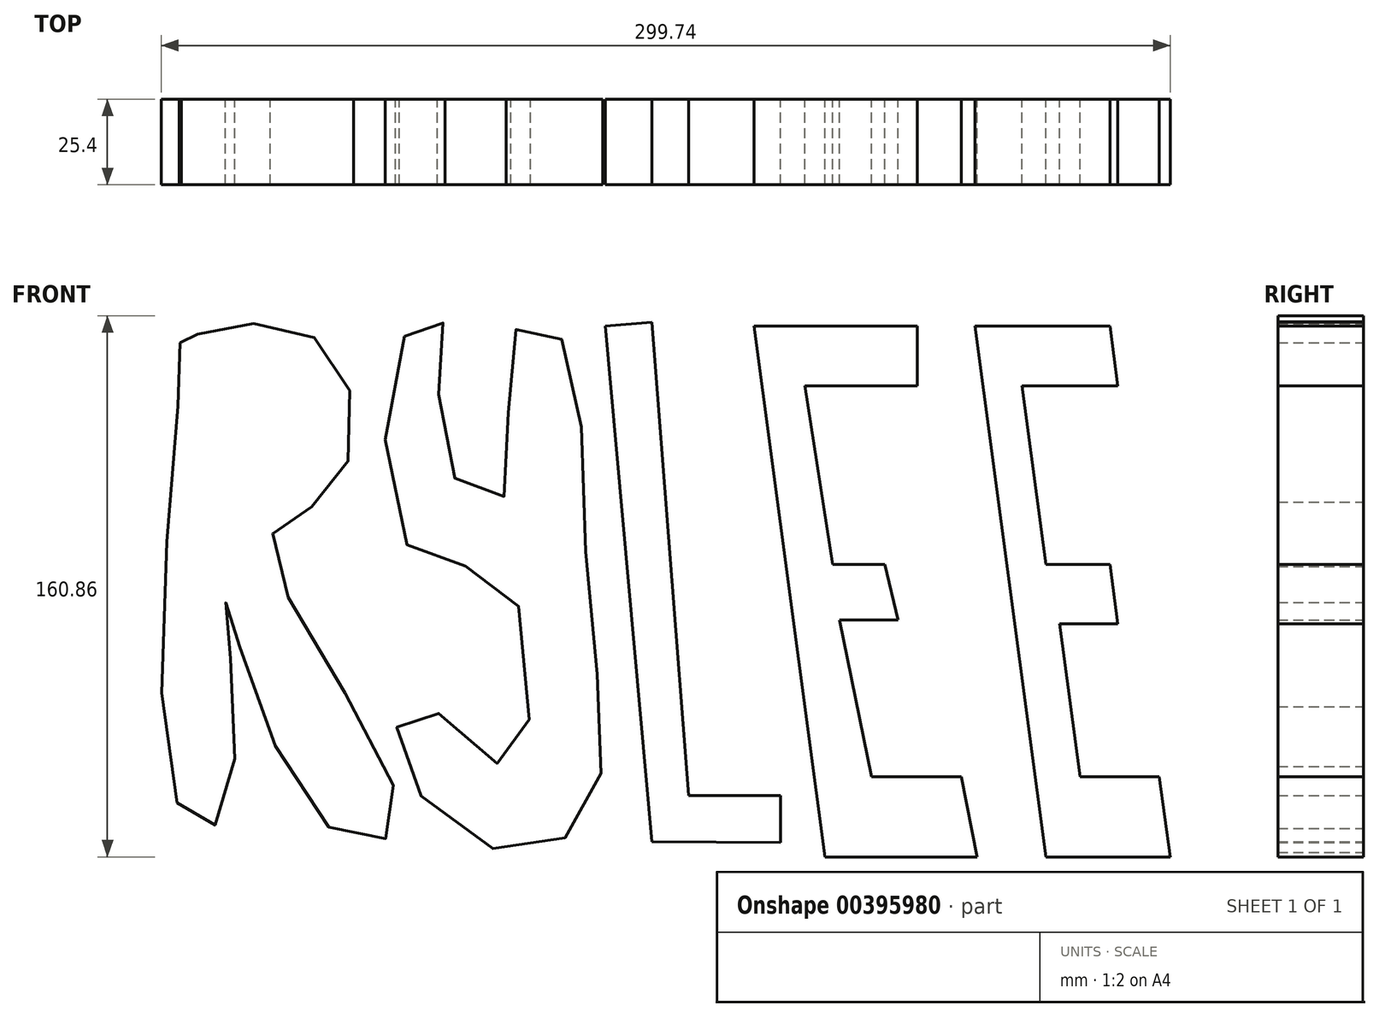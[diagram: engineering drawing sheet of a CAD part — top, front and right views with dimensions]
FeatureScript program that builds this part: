
annotation { "Feature Type Name" : "Feature", "Feature Type Description" : "" }
export const myFeature = defineFeature(function(context is Context, id is Id, definition is map)
    precondition{}
    {
        {
            var Q0;
            Q0=qCreatedBy(makeId("Front.planeOp"),FACE);
            var sketch = newSketch(context, id + "F0", { "sketchPlane" : qUnion([Q0])});
            skFitSpline(sketch, "E0", {"points": [v(-146.74, -62.42) * mm, v(-145.75, 74.33) * mm, v(-146.08, 74.37) * mm, v(-136.19, 78.37) * mm, v(-100.9, 71.57) * mm, v(-100.9, 29.89) * mm, v(-119.04, 14.58) * mm, v(-80.79, -66.82) * mm, v(-103.54, -67.91) * mm, v(-132.23, -2.87) * mm, v(-132.56, -65.5) * mm, v(-146.74, -62.42) * mm]});
            skSolve(sketch);
        }
        {
            var Q0;
            Q0=qCreatedBy(makeId("Front.planeOp"),FACE);
            var sketch = newSketch(context, id + "F1", { "sketchPlane" : qUnion([Q0])});
            skFitSpline(sketch, "E1", {"points": [v(-79.14, 76.34) * mm, v(-75.18, 10.48) * mm, v(-49.8, 4.41) * mm, v(-47.15, -51.23) * mm, v(-71.89, -34.31) * mm, v(-81.78, -42.74) * mm, v(-53.75, -75.77) * mm, v(-24.07, -64.67) * mm, v(-24.73, 3.42) * mm, v(-33.96, 77.39) * mm, v(-47.15, 76.5) * mm, v(-49.8, 28.36) * mm, v(-67.93, 41.14) * mm, v(-67.93, 80.76) * mm, v(-79.14, 76.34) * mm]});
            skSolve(sketch);
        }
        {
            var Q0;
            Q0=qCreatedBy(makeId("Front.planeOp"),FACE);
            var sketch = newSketch(context, id + "F2", { "sketchPlane" : qUnion([Q0])});
            skLineSegment(sketch, "E2", {"start": v(-19.46, 79.29) * mm, "end": v(-5.6, -74.23) * mm});
            skLineSegment(sketch, "E3", {"start": v(-5.94, -73.9) * mm, "end": v(32.65, -74.23) * mm});
            skLineSegment(sketch, "E4", {"start": v(32.65, -74.23) * mm, "end": v(32.65, -60.17) * mm});
            skLineSegment(sketch, "E5", {"start": v(32.65, -60.17) * mm, "end": v(5.28, -60.17) * mm});
            skLineSegment(sketch, "E6", {"start": v(5.28, -60.17) * mm, "end": v(-5.6, 80.52) * mm});
            skLineSegment(sketch, "E7", {"start": v(-5.6, 80.52) * mm, "end": v(-19.46, 79.29) * mm});
            skLineSegment(sketch, "E8", {"start": v(24.73, 79.29) * mm, "end": v(45.84, -78.47) * mm});
            skLineSegment(sketch, "E9", {"start": v(45.84, -78.47) * mm, "end": v(91.01, -78.47) * mm});
            skLineSegment(sketch, "E10", {"start": v(91.01, -78.47) * mm, "end": v(86.4, -54.63) * mm});
            skLineSegment(sketch, "E11", {"start": v(86.4, -54.63) * mm, "end": v(59.68, -54.63) * mm});
            skLineSegment(sketch, "E12", {"start": v(59.68, -54.63) * mm, "end": v(50.12, -8.08) * mm});
            skLineSegment(sketch, "E13", {"start": v(50.12, -8.08) * mm, "end": v(67.6, -8.08) * mm});
            skLineSegment(sketch, "E14", {"start": v(67.6, -8.08) * mm, "end": v(63.64, 8.43) * mm});
            skLineSegment(sketch, "E15", {"start": v(63.64, 8.43) * mm, "end": v(48.14, 8.43) * mm});
            skLineSegment(sketch, "E16", {"start": v(48.14, 8.43) * mm, "end": v(39.9, 61.58) * mm});
            skLineSegment(sketch, "E17", {"start": v(39.9, 61.58) * mm, "end": v(73.2, 61.58) * mm});
            skLineSegment(sketch, "E18", {"start": v(73.2, 61.58) * mm, "end": v(73.2, 79.29) * mm});
            skLineSegment(sketch, "E19", {"start": v(73.2, 79.29) * mm, "end": v(24.73, 79.29) * mm});
            skLineSegment(sketch, "E20", {"start": v(90.35, 79.29) * mm, "end": v(111.46, -78.47) * mm});
            skLineSegment(sketch, "E21", {"start": v(111.46, -78.47) * mm, "end": v(148.39, -78.47) * mm});
            skLineSegment(sketch, "E22", {"start": v(148.39, -78.47) * mm, "end": v(145.2, -54.63) * mm});
            skLineSegment(sketch, "E23", {"start": v(145.2, -54.63) * mm, "end": v(121.68, -54.63) * mm});
            skLineSegment(sketch, "E24", {"start": v(121.68, -54.63) * mm, "end": v(115.6, -9.2) * mm});
            skLineSegment(sketch, "E25", {"start": v(115.6, -9.2) * mm, "end": v(132.89, -9.2) * mm});
            skLineSegment(sketch, "E26", {"start": v(132.89, -9.2) * mm, "end": v(130.53, 8.43) * mm});
            skLineSegment(sketch, "E27", {"start": v(130.53, 8.43) * mm, "end": v(111.46, 8.43) * mm});
            skLineSegment(sketch, "E28", {"start": v(111.46, 8.43) * mm, "end": v(104.35, 61.58) * mm});
            skLineSegment(sketch, "E29", {"start": v(104.35, 61.58) * mm, "end": v(132.89, 61.58) * mm});
            skLineSegment(sketch, "E30", {"start": v(132.89, 61.58) * mm, "end": v(130.52, 79.29) * mm});
            skLineSegment(sketch, "E31", {"start": v(130.52, 79.29) * mm, "end": v(90.35, 79.29) * mm});
            skSolve(sketch);
        }
        {
            var Q0;
            Q0=makeQuery(id+"F0.imprint","IMPRINT",FACE,{"disambiguationData":[TD([[makeQuery(id+"F0.imprint","IMPRINT",EDGE,{"derivedFrom":sQuery(id+"F0.wireOp",EDGE,"E0")}),-1.0]])]});
            var Q1;
            Q1=makeQuery(id+"F1.imprint","IMPRINT",FACE,{"disambiguationData":[TD([[makeQuery(id+"F1.imprint","IMPRINT",EDGE,{"derivedFrom":sQuery(id+"F1.wireOp",EDGE,"E1")}),1.0]])]});
            var Q2;
            {var subQ0=sQuery(id+"F2.wireOp",EDGE,"E4");Q2=makeQuery(id+"F2.imprint","IMPRINT",FACE,{"disambiguationData":[TD([[makeQuery(id+"F2.imprint","IMPRINT",EDGE,{"derivedFrom":subQ0}),1.0]])]});}
            var Q3;
            Q3=makeQuery(id+"F2.imprint","IMPRINT",FACE,{"disambiguationData":[TD([[makeQuery(id+"F2.imprint","IMPRINT",EDGE,{"derivedFrom":sQuery(id+"F2.wireOp",EDGE,"E8")}),1.0]])]});
            var Q4;
            Q4=makeQuery(id+"F2.imprint","IMPRINT",FACE,{"disambiguationData":[TD([[makeQuery(id+"F2.imprint","IMPRINT",EDGE,{"derivedFrom":sQuery(id+"F2.wireOp",EDGE,"E20")}),1.0]])]});
            extrude(context, id + "F3", {"entities" : qUnion([Q0, Q1, Q2, Q3, Q4]), "depth" : 25.4 * mm});
        }
    });
